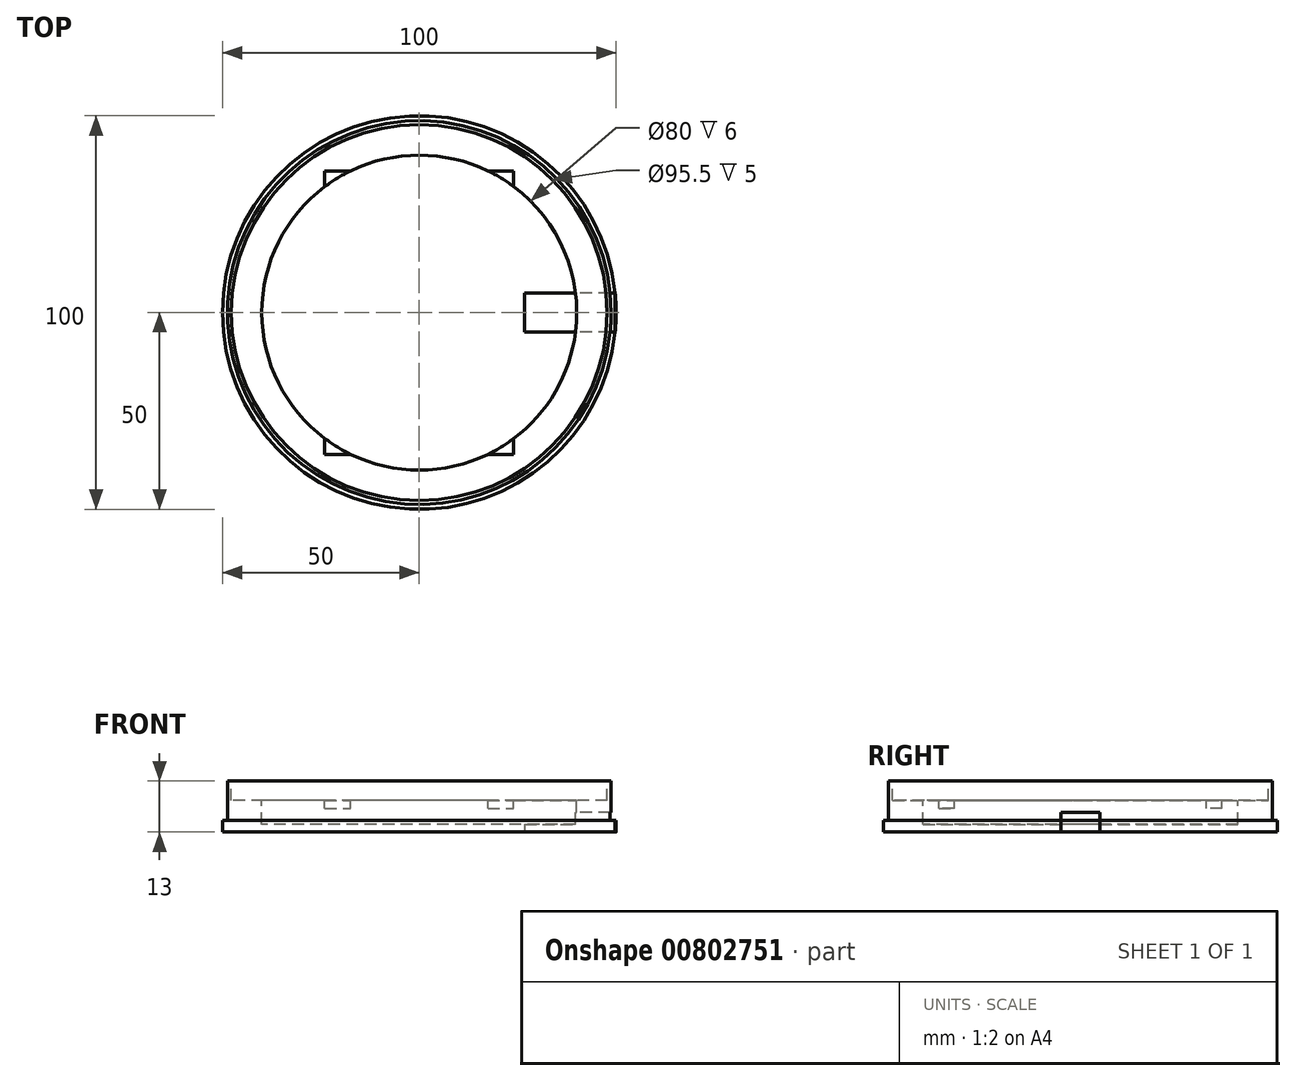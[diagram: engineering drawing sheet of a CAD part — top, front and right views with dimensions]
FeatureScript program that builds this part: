
annotation { "Feature Type Name" : "Feature", "Feature Type Description" : "" }
export const myFeature = defineFeature(function(context is Context, id is Id, definition is map)
    precondition{}
    {
        {
            var Q0;
            Q0=qCreatedBy(makeId("Top.planeOp"),FACE);
            var sketch = newSketch(context, id + "F0", { "sketchPlane" : qUnion([Q0])});
            skCircle(sketch, "E0", {"center": v(0, 0) * mm, "radius": 50 * mm});
            skSolve(sketch);
        }
        {
            var Q0;
            Q0 = qSketchRegion(id + "F0", true);
            extrude(context, id + "F1", {"entities" : qUnion([Q0]), "depth" : 3 * mm, "offsetDistance" : 25 * mm});
        }
        {
            var Q0;
            Q0=makeQuery(id+"F1.opExtrude","CAP_FACE",FACE,{"disambiguationData":[OSD([sQuery(id+"F0.wireOp",EDGE,"E0")])],"isStart":false});
            var sketch = newSketch(context, id + "F2", { "sketchPlane" : qUnion([Q0])});
            skCircle(sketch, "E1", {"center": v(0, 0) * mm, "radius": 48.75 * mm});
            skSolve(sketch);
        }
        {
            var Q0;
            Q0 = qSketchRegion(id + "F2", true);
            extrude(context, id + "F3", {"entities" : qUnion([Q0]), "operationType" : NewBodyOperationType.ADD, "depth" : 10 * mm, "offsetDistance" : 25 * mm});
        }
        {
            var Q0;
            Q0=makeQuery(id+"F3.opExtrude","CAP_FACE",FACE,{"disambiguationData":[OSD([sQuery(id+"F2.wireOp",EDGE,"E1")])],"isStart":false});
            var sketch = newSketch(context, id + "F4", { "sketchPlane" : qUnion([Q0])});
            skCircle(sketch, "E2", {"center": v(0, 0) * mm, "radius": 47.75 * mm});
            skSolve(sketch);
        }
        {
            var Q0;
            Q0 = qSketchRegion(id + "F4", true);
            extrude(context, id + "F5", {"entities" : qUnion([Q0]), "operationType" : NewBodyOperationType.REMOVE, "oppositeDirection" : true, "depth" : 5 * mm, "offsetDistance" : 25 * mm});
        }
        {
            var Q0;
            Q0=makeQuery(id+"F5.boolean.opBoolean","COPY",FACE,{"derivedFrom":makeQuery(id+"F5.opExtrude","CAP_FACE",FACE,{"disambiguationData":[OSD([sQuery(id+"F4.wireOp",EDGE,"E2")])],"isStart":false})});
            var sketch = newSketch(context, id + "F6", { "sketchPlane" : qUnion([Q0])});
            skCircle(sketch, "E3", {"center": v(0, 0) * mm, "radius": 40 * mm});
            skSolve(sketch);
        }
        {
            var Q0;
            Q0 = qSketchRegion(id + "F6", true);
            extrude(context, id + "F7", {"entities" : qUnion([Q0]), "operationType" : NewBodyOperationType.REMOVE, "oppositeDirection" : true, "depth" : 6 * mm, "offsetDistance" : 25 * mm});
        }
        {
            var Q0;
            Q0=makeQuery(id+"F5.boolean.opBoolean","COPY",FACE,{"derivedFrom":makeQuery(id+"F5.opExtrude","CAP_FACE",FACE,{"disambiguationData":[OSD([sQuery(id+"F4.wireOp",EDGE,"E2")])],"isStart":false})});
            var sketch = newSketch(context, id + "F8", { "sketchPlane" : qUnion([Q0])});
            skLineSegment(sketch, "E4.bottom", {"start": v(-24, 36) * mm, "end": v(24, 36) * mm});
            skLineSegment(sketch, "E4.top", {"start": v(-24, -36) * mm, "end": v(24, -36) * mm});
            skLineSegment(sketch, "E4.left", {"start": v(-24, 36) * mm, "end": v(-24, -36) * mm});
            skLineSegment(sketch, "E4.right", {"start": v(24, 36) * mm, "end": v(24, -36) * mm});
            skPoint(sketch, "E4.middle", {"position": v(0, 0) * mm});
            skSolve(sketch);
        }
        {
            var Q0;
            Q0 = qSketchRegion(id + "F8", true);
            extrude(context, id + "F9", {"entities" : qUnion([Q0]), "operationType" : NewBodyOperationType.REMOVE, "oppositeDirection" : true, "depth" : 2 * mm, "offsetDistance" : 25 * mm});
        }
        {
            var Q0;
            Q0=makeQuery(id+"F1.opExtrude","CAP_FACE",FACE,{"disambiguationData":[OSD([sQuery(id+"F0.wireOp",EDGE,"E0")])],"isStart":true});
            var sketch = newSketch(context, id + "F10", { "sketchPlane" : qUnion([Q0])});
            skLineSegment(sketch, "E5.bottom", {"start": v(49.75, 5) * mm, "end": v(26.75, 5) * mm});
            skLineSegment(sketch, "E5.top", {"start": v(49.75, -5) * mm, "end": v(26.75, -5) * mm});
            skLineSegment(sketch, "E5.left", {"start": v(49.75, 5) * mm, "end": v(49.75, -5) * mm});
            skLineSegment(sketch, "E5.right", {"start": v(26.75, 5) * mm, "end": v(26.75, -5) * mm});
            skPoint(sketch, "E5.middle", {"position": v(38.25, 0) * mm});
            skSolve(sketch);
        }
        {
            var Q0;
            Q0 = qSketchRegion(id + "F10", true);
            extrude(context, id + "F11", {"entities" : qUnion([Q0]), "operationType" : NewBodyOperationType.REMOVE, "oppositeDirection" : true, "depth" : 5 * mm, "offsetDistance" : 25 * mm});
        }
    });
